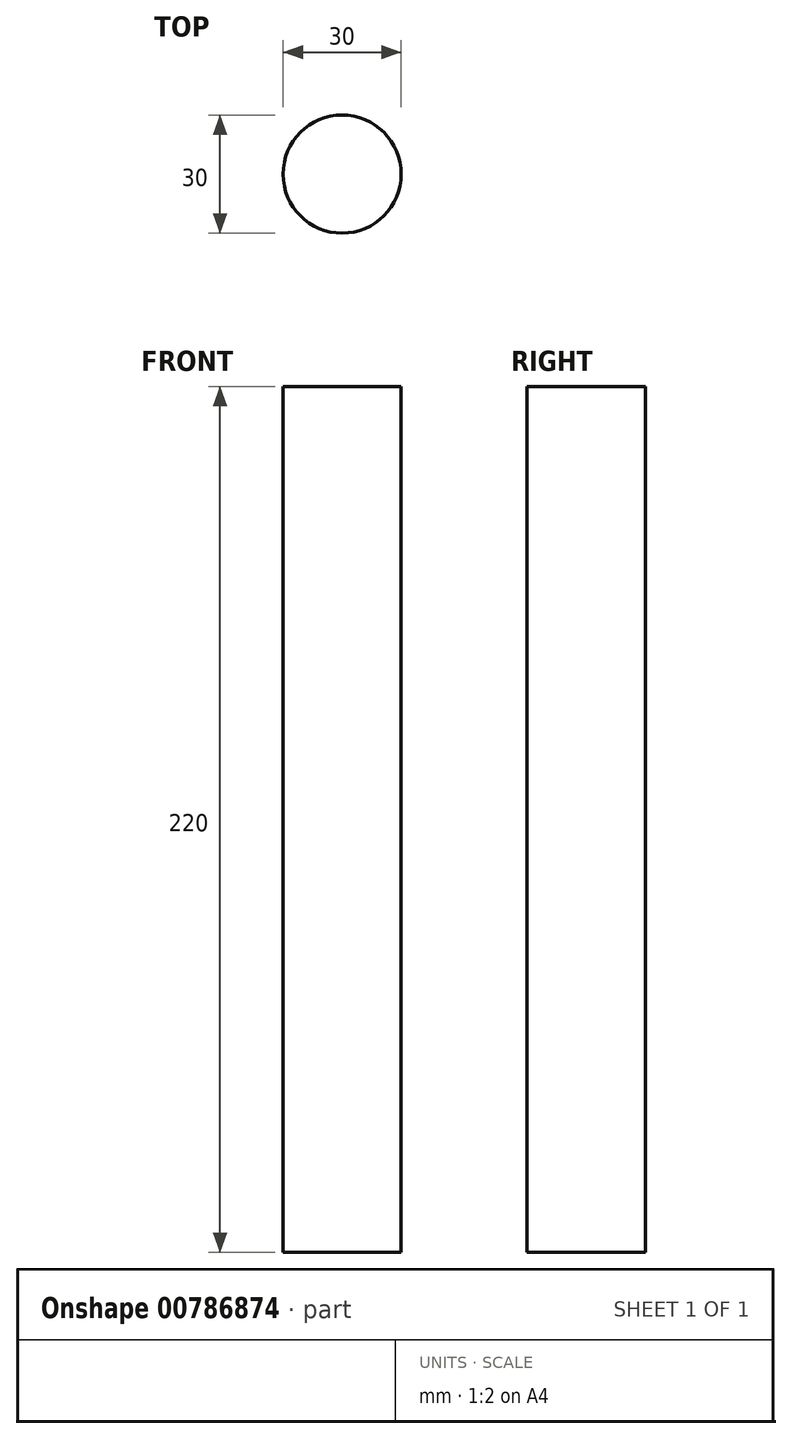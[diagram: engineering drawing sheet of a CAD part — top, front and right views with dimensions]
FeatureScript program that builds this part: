
annotation { "Feature Type Name" : "Feature", "Feature Type Description" : "" }
export const myFeature = defineFeature(function(context is Context, id is Id, definition is map)
    precondition{}
    {
        {
            var Q0;
            Q0=qCreatedBy(makeId("Top.planeOp"),FACE);
            var sketch = newSketch(context, id + "F0", { "sketchPlane" : qUnion([Q0])});
            skCircle(sketch, "E0", {"center": v(0, 0) * mm, "radius": 15 * mm});
            skSolve(sketch);
        }
        {
            var Q0;
            Q0 = qSketchRegion(id + "F0", true);
            extrude(context, id + "F1", {"entities" : qUnion([Q0]), "depth" : 220 * mm, "offsetDistance" : 25 * mm});
        }
    });
